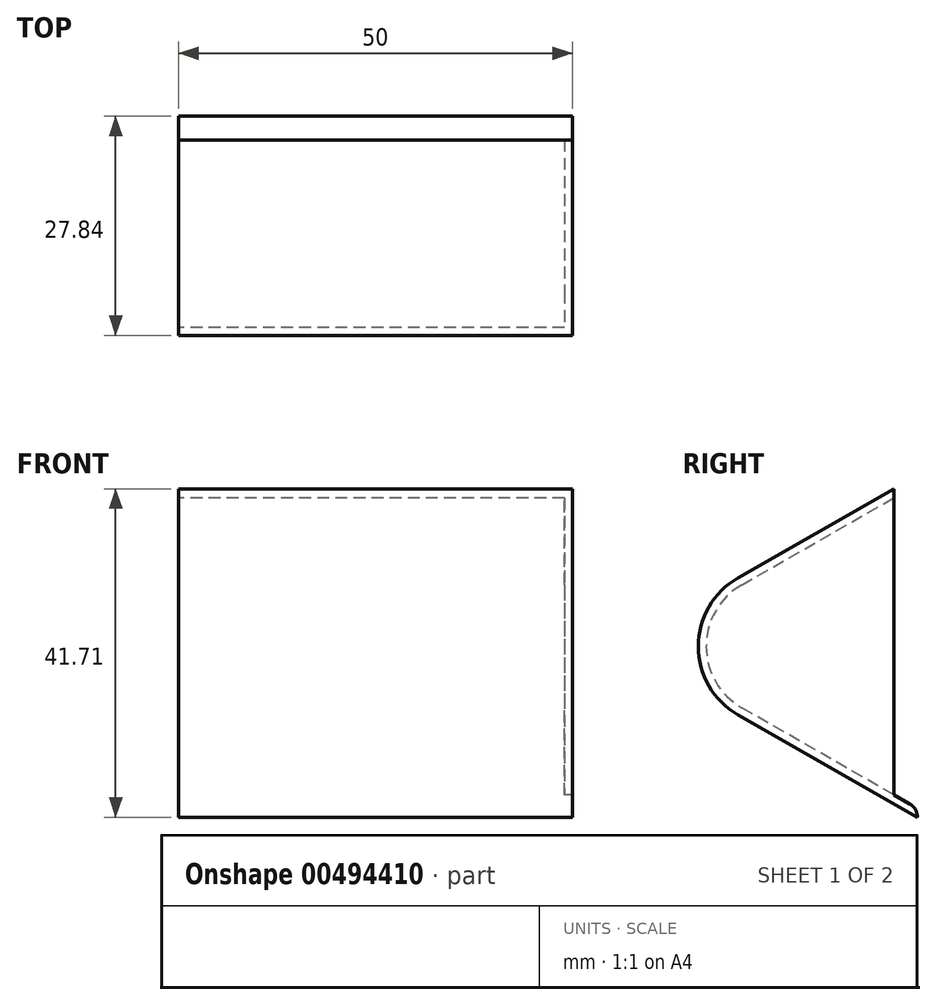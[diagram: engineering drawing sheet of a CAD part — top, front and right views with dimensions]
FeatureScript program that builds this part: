
annotation { "Feature Type Name" : "Feature", "Feature Type Description" : "" }
export const myFeature = defineFeature(function(context is Context, id is Id, definition is map)
    precondition{}
    {
        {
            var Q0;
            Q0=qCreatedBy(makeId("Right.planeOp"),FACE);
            var sketch = newSketch(context, id + "F0", { "sketchPlane" : qUnion([Q0])});
            skCircle(sketch, "E0", {"center": v(0, 0) * mm, "radius": 1.5 * mm});
            skLineSegment(sketch, "E1", {"start": v(0, 0) * mm, "end": v(0, -40) * mm});
            skLineSegment(sketch, "E2", {"start": v(0, -40) * mm, "end": v(-19.8, -28.68) * mm});
            skLineSegment(sketch, "E3", {"start": v(-19.8, -11.32) * mm, "end": v(-1.3, -0.74) * mm});
            skPoint(sketch, "E4.visualSharp", {"position": v(-35, -20) * mm});
            skArc(sketch, "E4.filletArc", {"start": v(-19.8, -11.32) * mm, "mid": v(-24.84, -20) * mm, "end": v(-19.8, -28.68) * mm});
            skLineSegment(sketch, "E5.0", {"start": v(-19.3, -12.19) * mm, "end": v(-0.47, -1.42) * mm});
            skArc(sketch, "E5.1", {"start": v(-19.3, -12.19) * mm, "mid": v(-23.84, -20) * mm, "end": v(-19.3, -27.81) * mm});
            skLineSegment(sketch, "E5.2", {"start": v(0, -38.85) * mm, "end": v(-19.3, -27.81) * mm});
            skLineSegment(sketch, "E6", {"start": v(-14.84, -20) * mm, "end": v(-24.84, -20) * mm, "construction": true});
            skLineSegment(sketch, "E7", {"start": v(0, -40) * mm, "end": v(3, -41.71) * mm});
            skLineSegment(sketch, "E8", {"start": v(0, -38.85) * mm, "end": v(3, -40.56) * mm});
            skLineSegment(sketch, "E9", {"start": v(3, -40.56) * mm, "end": v(3, -41.71) * mm});
            skLineSegment(sketch, "E10", {"start": v(0, 0) * mm, "end": v(-1.3, -0.74) * mm});
            skLineSegment(sketch, "E11", {"start": v(0, 0) * mm, "end": v(-0.74, 1.3) * mm});
            skLineSegment(sketch, "E12", {"start": v(-0.74, 1.3) * mm, "end": v(-16.86, -7.9) * mm});
            skLineSegment(sketch, "E13", {"start": v(-19.46, -10.05) * mm, "end": v(-22.41, -13.46) * mm});
            skPoint(sketch, "E14.visualSharp", {"position": v(-18.34, -8.75) * mm});
            skArc(sketch, "E14.filletArc", {"start": v(-16.86, -7.9) * mm, "mid": v(-18.25, -8.87) * mm, "end": v(-19.46, -10.05) * mm});
            skLineSegment(sketch, "E15", {"start": v(-0.47, -1.42) * mm, "end": v(0, -1.15) * mm});
            skSolve(sketch);
        }
        {
            var Q0;
            {var subQ1=sQuery(id+"F0.wireOp",EDGE,"E2");Q0=makeQuery(id+"F0.imprint","IMPRINT",FACE,{"disambiguationData":[TD([[makeQuery(id+"F0.imprint","IMPRINT",EDGE,{"derivedFrom":subQ1}),-1.0]])]});}
            var Q1;
            {var subQ0=sQuery(id+"F0.wireOp",EDGE,"E10");Q1=makeQuery(id+"F0.imprint","IMPRINT",FACE,{"disambiguationData":[TD([[makeQuery(id+"F0.imprint","IMPRINT",EDGE,{"derivedFrom":subQ0}),1.0]])]});}
            extrude(context, id + "F1", {"entities" : qUnion([Q0, Q1]), "depth" : 25 * mm, "hasSecondDirection" : true, "secondDirectionOppositeDirection" : true, "secondDirectionDepth" : 25 * mm});
        }
        {
            var Q0;
            {var subQ0=sQuery(id+"F0.wireOp",EDGE,"E7");Q0=makeQuery(id+"F0.imprint","IMPRINT",FACE,{"disambiguationData":[TD([[makeQuery(id+"F0.imprint","IMPRINT",EDGE,{"derivedFrom":subQ0}),1.0]])]});}
            extrude(context, id + "F2", {"entities" : qUnion([Q0]), "operationType" : NewBodyOperationType.ADD, "depth" : 25 * mm, "hasSecondDirection" : true, "secondDirectionOppositeDirection" : true, "secondDirectionDepth" : 25 * mm});
        }
        {
            var Q0;
            Q0=makeQuery(id+"F2.opExtrude","SWEPT_EDGE",EDGE,{"disambiguationData":[OSD([sQuery(id+"F0.wireOp",EDGE,"E8"),sQuery(id+"F0.wireOp",EDGE,"E9")])]});
            fillet(context, id + "F3", {"entities" : qUnion([Q0]), "radius" : 2 * mm, "tangentPropagation" : true, "allowEdgeOverflow" : false});
        }
        {
            var Q0;
            {var subQ0=sQuery(id+"F0.wireOp",EDGE,"E5.0");Q0=makeQuery(id+"F0.imprint","IMPRINT",FACE,{"disambiguationData":[TD([[makeQuery(id+"F0.imprint","IMPRINT",EDGE,{"derivedFrom":subQ0}),-1.0]])]});}
            var Q1;
            {var subQ0=sQuery(id+"F0.wireOp",EDGE,"E15");Q1=makeQuery(id+"F0.imprint","IMPRINT",FACE,{"disambiguationData":[TD([[makeQuery(id+"F0.imprint","IMPRINT",EDGE,{"derivedFrom":subQ0}),-1.0]])]});}
            extrude(context, id + "F4", {"entities" : qUnion([Q0, Q1]), "operationType" : NewBodyOperationType.ADD, "depth" : 25 * mm, "hasSecondDirection" : true, "secondDirectionOppositeDirection" : false, "secondDirectionDepth" : 24 * mm});
        }
    });
